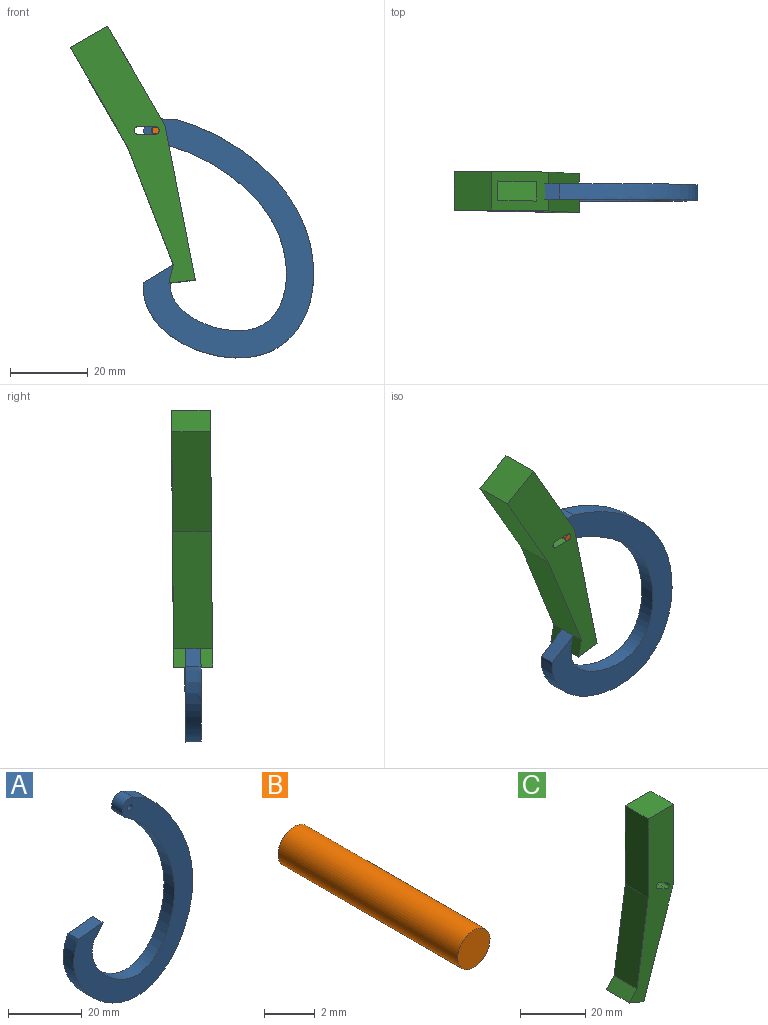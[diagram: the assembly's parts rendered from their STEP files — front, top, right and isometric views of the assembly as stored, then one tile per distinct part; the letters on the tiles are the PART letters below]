
ASSEMBLY  parts=3 mates=2
PART A: 10 faces, bbox 45.6x4x67 mm
  f0: extruded ~52.12x31.6mm, area 375.1mm2, adj f1,f7,f8,f9
  f1: plane 4x3.69mm, normal (0.79,0,-0.62), area 18.7mm2, adj f0,f2,f8,f9
  f2: plane 9.43x4mm, normal (-0.1,0,1), area 37.9mm2, adj f1,f3,f8,f9
  f3: extruded ~64.46x45.46mm, area 498.6mm2, adj f2,f4,f8,f9
  f4: plane 4.59x4mm, normal (0.44,0,0.9), area 20.4mm2, adj f3,f5,f8,f9
  f5: cylinder r=3mm len=5.3mm, axis (0,1,0), area 34.8mm2, adj f4,f7,f8,f9
  f6: cylinder r=1mm len=4mm, axis (0,1,0), area 25.1mm2, adj f8,f9
  f7: plane 4x3.25mm, normal (-0.61,0,-0.79), area 16.5mm2, adj f0,f5,f8,f9
  f8: plane 67.03x45.65mm, normal (0,-1,0), area 818.4mm2, adj f0,f1,f2,f3,f4,f5,f6,f7
  f9: plane 67.03x45.65mm, normal (0,1,0), area 818.4mm2, adj f0,f1,f2,f3,f4,f5,f6,f7
PART B: 3 faces, bbox 1.8x10x1.8 mm
  f0: cylinder r=0.9mm len=10mm, axis (0,1,0), area 56.5mm2, adj f1,f2
  f1: plane 1.8x1.8mm, normal (0,-1,0), area 2.5mm2, adj f0
  f2: plane 1.8x1.8mm, normal (0,1,0), area 2.5mm2, adj f0
PART C: 18 faces, bbox 19.3x10x67.9 mm
  f0: plane 29.59x10mm, normal (1,0,0), area 195.3mm2, adj f5,f6,f11,f12,f13,f15,f16,f17
  f1: cylinder r=1mm len=10mm, axis (0,1,0), area 31.4mm2, adj f2,f10,f11,f12
  f2: plane 10x3.9mm, normal (-0.5,0,-0.87), area 45mm2, adj f1,f3,f11,f12
  f3: cylinder r=1mm len=10mm, axis (0,1,0), area 31.4mm2, adj f2,f10,f11,f12
  f4: plane 10x6.3mm, normal (-0.39,0,-0.92), area 68.3mm2, adj f5,f9,f11,f12
  f5: plane 38.26x12.96mm, normal (0.95,0,-0.32), area 404mm2, adj f0,f4,f11,f12
  f6: plane 11.05x10mm, normal (0,0,1), area 110.5mm2, adj f0,f7,f11,f12
  f7: plane 29.59x10mm, normal (-1,0,0), area 295.9mm2, adj f6,f8,f11,f12
  f8: plane 31.99x10mm, normal (-0.99,0,0.15), area 323.5mm2, adj f7,f9,f11,f12
  f9: plane 10x3.62mm, normal (-0.73,0,0.68), area 49.5mm2, adj f4,f8,f11,f12
  f10: plane 10x3.9mm, normal (0.5,0,0.87), area 45mm2, adj f1,f3,f11,f12
  f11: plane 67.85x19.26mm, normal (0,-1,0), area 603.9mm2, adj f0,f1,f2,f3,f4,f5,f6,f7
  f12: plane 67.85x19.26mm, normal (0,1,0), area 603.9mm2, adj f0,f1,f2,f3,f4,f5,f6,f7
  f13: plane 9.56x5mm, normal (0,0,-1), area 47.8mm2, adj f0,f14,f16,f17
  f14: plane 11.78x5mm, normal (1,0,0), area 58.9mm2, adj f13,f15,f16,f17
  f15: plane 9.56x8.35mm, normal (0.66,0,0.75), area 63.4mm2, adj f0,f14,f16,f17
  f16: plane 20.12x9.56mm, normal (0,-1,0), area 152.4mm2, adj f0,f13,f14,f15
  f17: plane 20.12x9.56mm, normal (0,1,0), area 152.4mm2, adj f0,f13,f14,f15
PLACE A rot(axis=(-0.02,-1,0.02),25.6deg) t=(17.79,-6.74,9.6)mm
PLACE B rot(axis=(0,-1,0.01),89.8deg) t=(0.72,-3.49,42.15)mm
PLACE C rot(axis=(-0.02,-1,0.01),29.8deg) t=(15.39,-3.69,15.17)mm fixed
MATE cylindrical B.f0 <-> A.f5  axis (0,-1,0.01) through (0.77,-13.49,42.25)mm
MATE pin_slot C.f1 <-> B.f0  axis (0,-1,0.01) through (-3.73,-13.51,42.27)mm
